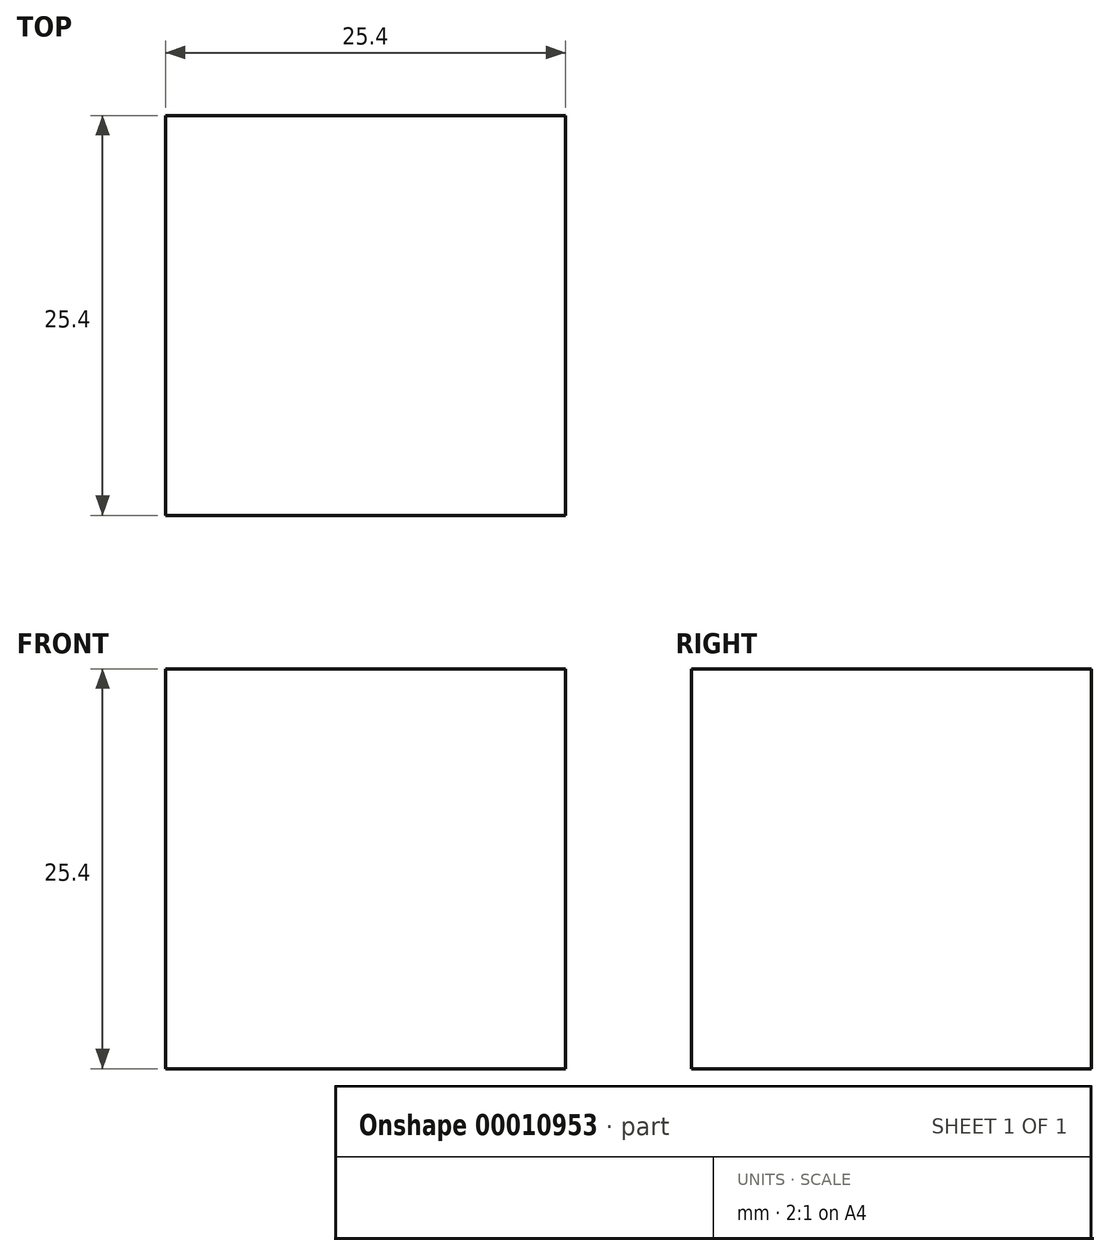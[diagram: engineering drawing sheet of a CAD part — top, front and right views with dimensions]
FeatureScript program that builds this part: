
annotation { "Feature Type Name" : "Feature", "Feature Type Description" : "" }
export const myFeature = defineFeature(function(context is Context, id is Id, definition is map)
    precondition{}
    {
        {
            var Q0;
            Q0=qCreatedBy(makeId("Top.planeOp"),FACE);
            var sketch = newSketch(context, id + "F0", { "sketchPlane" : qUnion([Q0])});
            skLineSegment(sketch, "E0.rect.bottom", {"start": v(12.7, -12.7) * mm, "end": v(-12.7, -12.7) * mm});
            skLineSegment(sketch, "E0.rect.top", {"start": v(12.7, 12.7) * mm, "end": v(-12.7, 12.7) * mm});
            skLineSegment(sketch, "E0.rect.left", {"start": v(12.7, -12.7) * mm, "end": v(12.7, 12.7) * mm});
            skLineSegment(sketch, "E0.rect.right", {"start": v(-12.7, -12.7) * mm, "end": v(-12.7, 12.7) * mm});
            skPoint(sketch, "E0.rect.middle", {"position": v(0, 0) * mm});
            skSolve(sketch);
        }
        {
            var Q0;
            Q0=makeQuery(id+"F0.imprint","IMPRINT",FACE,{"disambiguationData":[TD([[makeQuery(id+"F0.imprint","IMPRINT",EDGE,{"derivedFrom":sQuery(id+"F0.wireOp",EDGE,"E0.rect.bottom")}),-1.0]])]});
            extrude(context, id + "F1", {"entities" : qUnion([Q0]), "depth" : 25.4 * mm});
        }
    });
